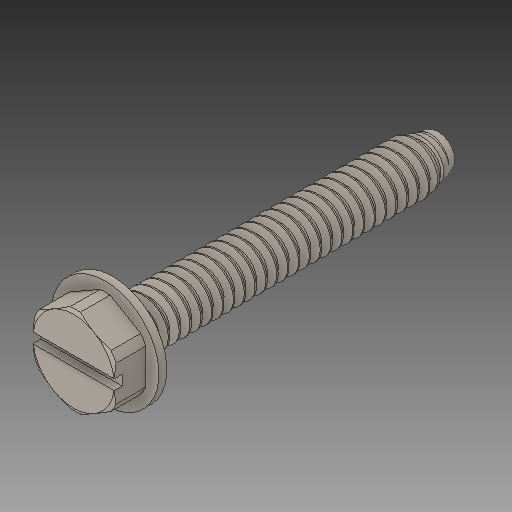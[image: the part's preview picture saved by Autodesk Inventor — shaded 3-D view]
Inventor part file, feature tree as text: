
AUTODESK INVENTOR PART (.ipt)
format: ipt  version: 2019 (Build 230136000, 136)  size: 807,424 bytes
history: native  units: in
note: dims shown in document units (in); Inventor stores cm internally (conversion verified against a paired STEP export)
features: extrude x1
ambient origin geometry x8: Origin, YZ Plane, XZ Plane, XY Plane, X Axis, Y Axis, Z Axis, Center Point
bodies: Solid1 (feature_tree)
feature tree (1):
  extrude  "Extrude4"  [1 undecoded]
note: 1 required parameter value undecoded (feature->parameter linkage not recoverable at this tier; creation-order binding heuristic only, values carry confidence <= 0.55)
